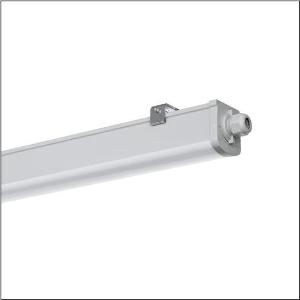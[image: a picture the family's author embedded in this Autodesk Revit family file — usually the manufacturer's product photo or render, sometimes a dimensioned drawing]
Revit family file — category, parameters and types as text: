
# Revit family: monsun_r__31_51fa207k430b_6f38
name_source: partatom
category: Lighting Fixtures
units: mm (PartAtom-declared; Revit-internal decimal feet)

## family parameters
Cut with Voids When Loaded = No
Host = Face
Light Source = No
Part Type = Normal
Room Calculation Point = No
Round Connector Dimension = Use Diameter
Shared = No

## types (1)
- Monsun® 31 (1 x LED, 3000 lm, 22 W, 4000K)
    Apparent Load = 22 VA
    CIE Flux Codes = 42 72 91 92 100
    Color Rendering = 80
    Color Temperature = 4000K
    Default Elevation = 1800 mm
    Description = Monsun® 31, damp-proof luminaire, primary optical cover: diffuser, of PC, frosted, light emission: direct distribution, primary light characteristic: symmetric, installation type: surface-mounted, LED, rated luminous flux: 3.000lm, luminous efficacy: 136lm/W, light colour: 840, colour temperature: 4000K, control gear: ECG, with terminal, 3+1-pole, max. 2.5mm², through-wiring: 3x 2.5mm² + 1x 1.5mm², mains connection: 220..240V, AC, 50/60Hz, rated input power: 22W, housing, luminaire housing, of PC, light grey (RAL 7035), length: 1.158mm, width: 68mm, height: 76mm, protection rating (complete): IP66, insulation class (complete): insulation class II (safety insulation), certification: CE, ENEC, UKCA, protection symbol: D, impact resistance: IK08, permissible operating ambient temperature: -20..+40°C, corresponds to IFS (International Featured Standards) requirements for safety and quality in the food industry, contact your sales advisor before using the luminaires in applications with unclear chemical exposure, large temperature fluctuations or condensation-forming humidity, packaging unit: 1 piece
    Height = 77 mm
    Lamp = 1 x LED
    Lamp Light Flux = 3000 lm
    Lamp Power = 22 W
    Lamp count = 1
    Length = 1218 mm
    Luminous efficacy = 136 lm/W
    Manufacturer = Siteco
    ModVariant = No
    Model = 51FA207K430B
    Mounting Place = Ceiling
    Mounting Type = Surface mounted
    Number of Poles = 1
    OnlyDefault = Yes
    Power Factor = 1
    Product Name = Monsun® 31
    Product group = damp-proof luminaire
    ProductGroupID = 300
    Protection Class = Protection class II
    Protection Degree = IP 66
    RLX_Detail_Level = 1
    RLX_Emergency_Light_Flux = 0 lm
    RLX_Emergency_Type = 0
    RLX_Emergency_Type_DB = No
    RlxData = <blob elided: 32993 chars, md5=b5b8cd13>
    Socket = socket
    Standby Power = 0 W
    System Light Flux = 3000 lm
    System Power = 22 W
    Type Comments = Product without accessories
    Type Image = l_1006174.jpg
    URL = http://relux.com
    VarID = ---
    Voltage = 0 V
    Weight = 0.00 kg
    Width = 69 mm

## geometry (parser evidence)
native form markers: Blend x4, Sweep x11
no freeform markers — native parametric forms only
